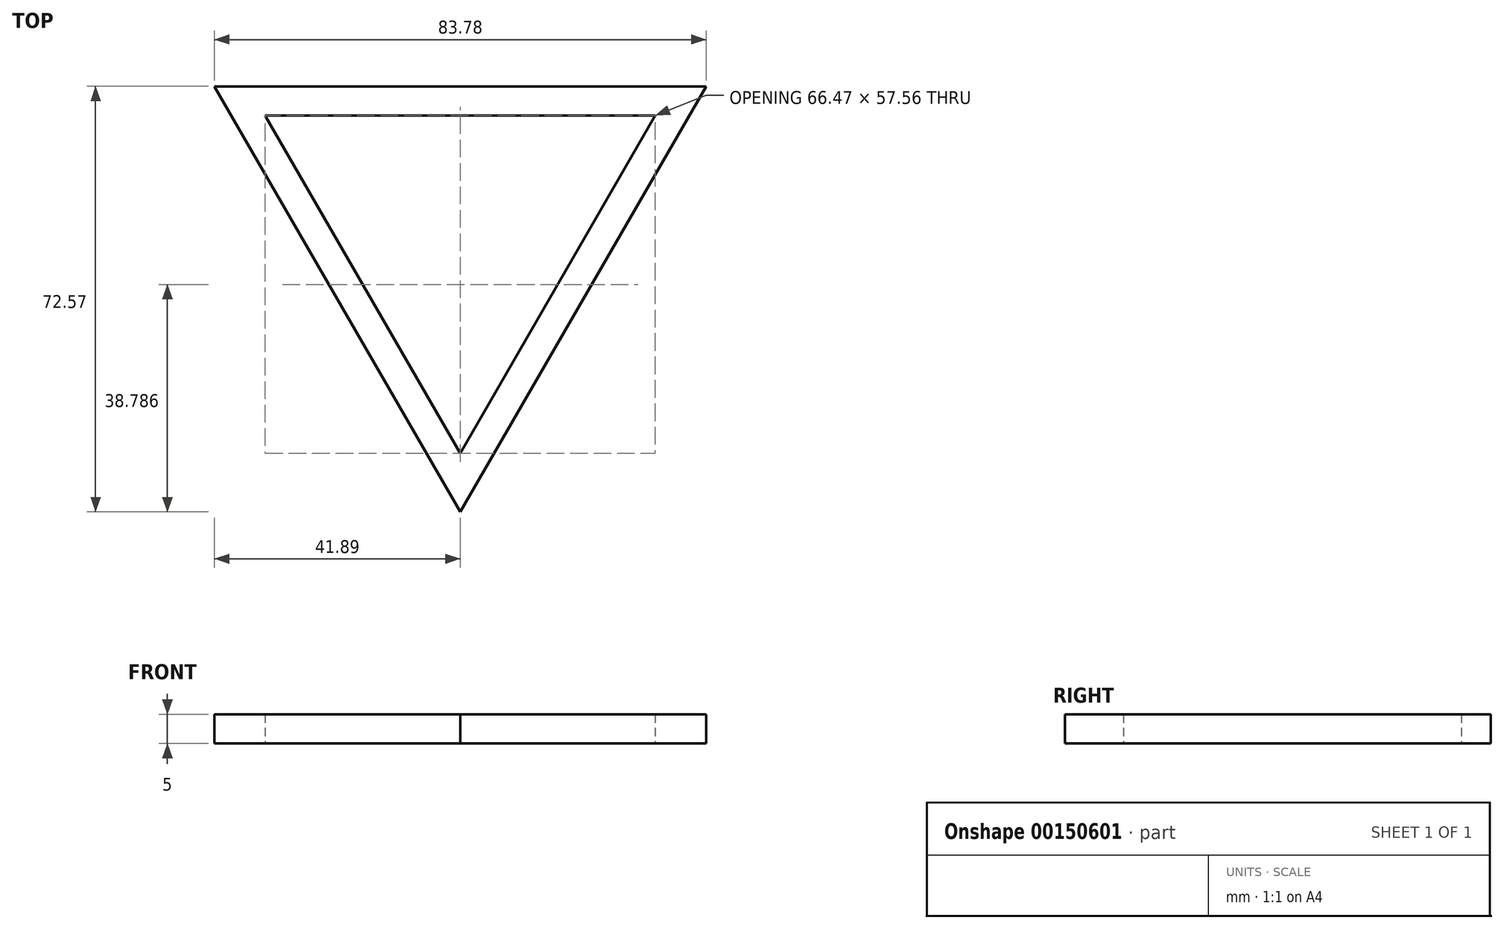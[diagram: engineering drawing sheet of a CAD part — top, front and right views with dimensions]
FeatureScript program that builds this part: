
annotation { "Feature Type Name" : "Feature", "Feature Type Description" : "" }
export const myFeature = defineFeature(function(context is Context, id is Id, definition is map)
    precondition{}
    {
        {
            var Q0;
            Q0=qCreatedBy(makeId("Top.planeOp"),FACE);
            var sketch = newSketch(context, id + "F0", { "sketchPlane" : qUnion([Q0])});
            skLineSegment(sketch, "E0", {"start": v(-41.9, 35.3) * mm, "end": v(41.9, 35.3) * mm});
            skLineSegment(sketch, "E1", {"start": v(41.9, 35.3) * mm, "end": v(0, -37.26) * mm});
            skLineSegment(sketch, "E2", {"start": v(0, -37.26) * mm, "end": v(-41.9, 35.3) * mm});
            skLineSegment(sketch, "E3.0", {"start": v(33.23, 30.3) * mm, "end": v(0, -27.26) * mm});
            skLineSegment(sketch, "E3.1", {"start": v(-33.23, 30.3) * mm, "end": v(33.23, 30.3) * mm});
            skLineSegment(sketch, "E3.2", {"start": v(0, -27.26) * mm, "end": v(-33.23, 30.3) * mm});
            skSolve(sketch);
        }
        {
            var Q0;
            Q0=makeQuery(id+"F0.imprint","IMPRINT",FACE,{"disambiguationData":[TD([[makeQuery(id+"F0.imprint","IMPRINT",EDGE,{"derivedFrom":sQuery(id+"F0.wireOp",EDGE,"E0")}),-1.0]])]});
            extrude(context, id + "F1", {"entities" : qUnion([Q0]), "depth" : 5 * mm});
        }
    });
